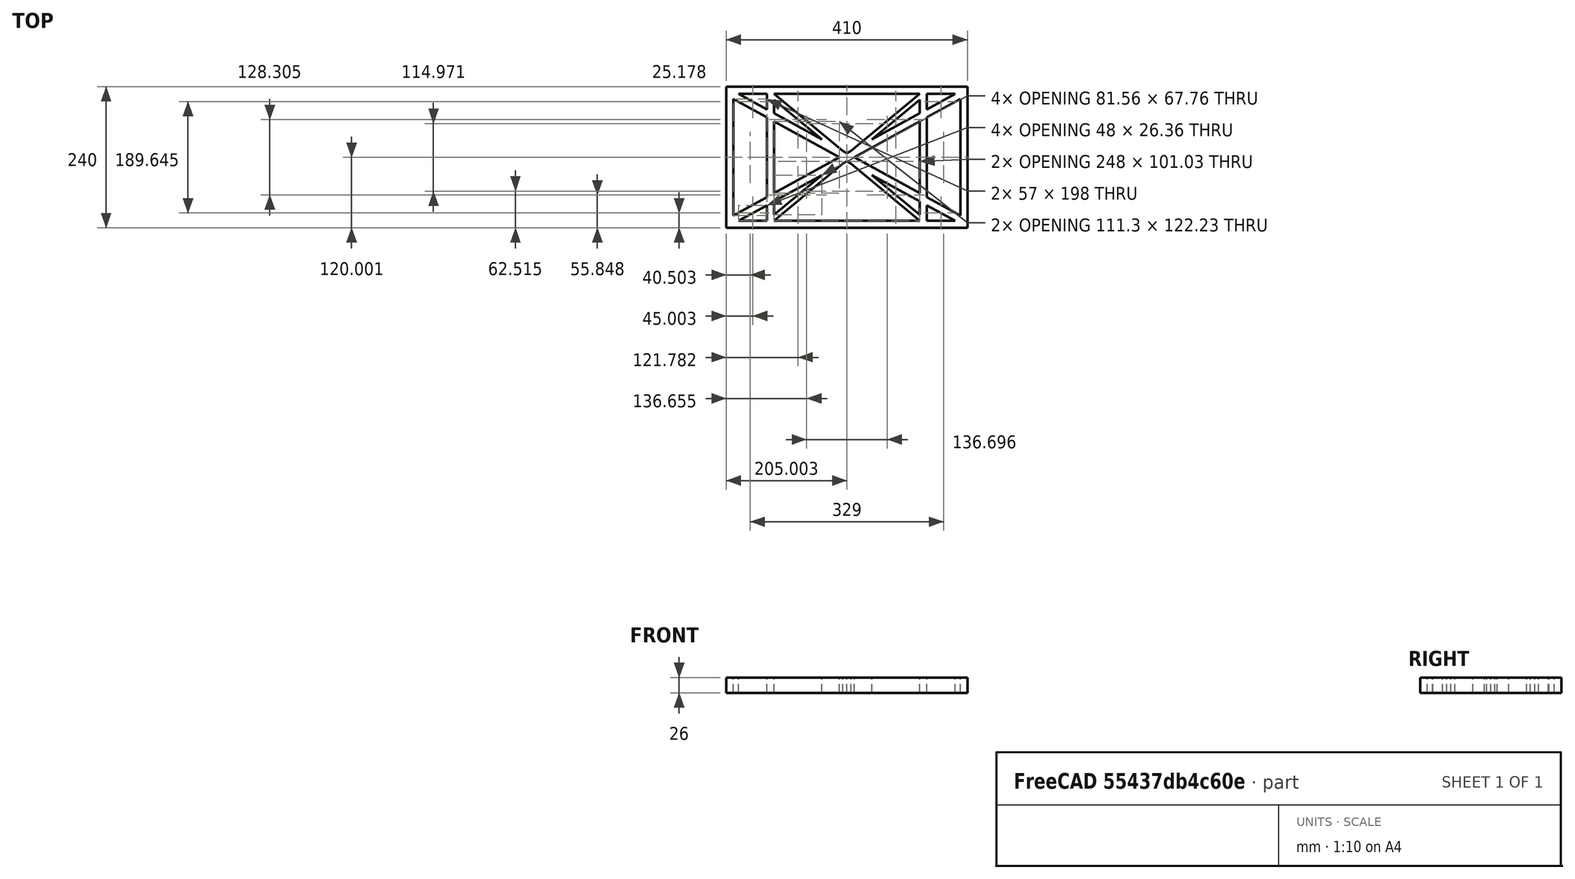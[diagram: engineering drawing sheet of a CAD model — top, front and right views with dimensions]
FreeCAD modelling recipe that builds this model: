
FCSTD DOCUMENT  (FreeCAD 0.19R0.19.2)
Label: laptopStand018
License: All rights reserved
LicenseURL: http://en.wikipedia.org/wiki/All_rights_reserved
objects: Sketcher::SketchObject×3, Part::Extrusion×1
note: 4 computed .brp shape members not serialized (recipe doc carries the construction recipe); baked Part::Feature solids carry a one-line shape summary decoded from their .brp

FEATURE [Sketcher::SketchObject] Sketch
  FullyConstrained = true
  sketch-geometry (52):
    g0: LineSegment StartX=-22.9272 StartY=136.221 StartZ=0 EndX=-22.9272 EndY=-103.779 EndZ=0
    g1: LineSegment StartX=-22.9272 StartY=136.221 StartZ=0 EndX=387.073 EndY=136.221 EndZ=0
    g2: LineSegment StartX=-22.9272 StartY=-103.779 StartZ=0 EndX=387.073 EndY=-103.779 EndZ=0
    g3: LineSegment StartX=387.073 StartY=136.221 StartZ=0 EndX=387.073 EndY=-103.779 EndZ=0
    g4: LineSegment StartX=375.073 StartY=115.221 StartZ=0 EndX=318.073 EndY=83.9235 EndZ=0
    g5: LineSegment StartX=-10.9272 StartY=-82.7794 StartZ=0 EndX=46.0728 EndY=-51.4823 EndZ=0
    g6: LineSegment StartX=-1.92719 StartY=124.221 StartZ=0 EndX=46.0728 EndY=97.8651 EndZ=0
    g7: LineSegment StartX=366.073 StartY=-91.7794 StartZ=0 EndX=318.073 EndY=-65.424 EndZ=0
    g8: LineSegment StartX=-10.9272 StartY=115.221 StartZ=0 EndX=-10.9272 EndY=-82.7794 EndZ=0
    g9: LineSegment StartX=375.073 StartY=-82.7794 StartZ=0 EndX=375.073 EndY=115.221 EndZ=0
    g10: LineSegment StartX=-1.92719 StartY=-91.7794 StartZ=0 EndX=46.0728 EndY=-91.7794 EndZ=0
    g11: LineSegment StartX=318.073 StartY=124.221 StartZ=0 EndX=366.073 EndY=124.221 EndZ=0
    g12: LineSegment StartX=306.073 StartY=-81.8102 StartZ=0 EndX=224.513 EndY=-14.0532 EndZ=0
    g13: LineSegment StartX=58.0728 StartY=114.251 StartZ=0 EndX=139.632 EndY=46.4944 EndZ=0
    g14: LineSegment StartX=306.073 StartY=124.221 StartZ=0 EndX=189.124 EndY=27.0628 EndZ=0
    g15: LineSegment StartX=58.0728 StartY=-91.7794 StartZ=0 EndX=175.022 EndY=5.37834 EndZ=0
    g16: LineSegment StartX=46.0728 StartY=124.221 StartZ=0 EndX=46.0728 EndY=97.8651 EndZ=0
    g17: LineSegment StartX=58.0728 StartY=-81.8102 StartZ=0 EndX=58.0728 EndY=-58.8351 EndZ=0
    g18: LineSegment StartX=318.073 StartY=124.221 StartZ=0 EndX=318.073 EndY=97.8651 EndZ=0
    g19: LineSegment StartX=306.073 StartY=114.251 StartZ=0 EndX=306.073 EndY=91.2763 EndZ=0
    g20: LineSegment StartX=182.073 StartY=23.1914 StartZ=0 EndX=189.124 EndY=27.0628 EndZ=0
    g21: LineSegment StartX=182.073 StartY=9.24976 StartZ=0 EndX=175.022 EndY=5.37834 EndZ=0
    g22: LineSegment StartX=224.513 StartY=46.4944 StartZ=0 EndX=306.073 EndY=114.251 EndZ=0
    g23: LineSegment StartX=175.022 StartY=27.0628 StartZ=0 EndX=58.0728 EndY=124.221 EndZ=0
    g24: LineSegment StartX=169.377 StartY=16.2206 StartZ=0 EndX=58.0728 EndY=77.3346 EndZ=0
    g25: LineSegment StartX=139.632 StartY=-14.0532 StartZ=0 EndX=58.0728 EndY=-81.8102 EndZ=0
    g26: LineSegment StartX=194.768 StartY=16.2206 StartZ=0 EndX=306.073 EndY=-44.8935 EndZ=0
    g27: LineSegment StartX=224.513 StartY=46.4944 StartZ=0 EndX=306.073 EndY=91.2763 EndZ=0
    g28: LineSegment StartX=175.022 StartY=27.0628 StartZ=0 EndX=182.073 EndY=23.1914 EndZ=0
    g29: LineSegment StartX=139.632 StartY=-14.0532 StartZ=0 EndX=58.0728 EndY=-58.8351 EndZ=0
    g30: LineSegment StartX=189.124 StartY=5.37834 StartZ=0 EndX=182.073 EndY=9.24976 EndZ=0
    g31: LineSegment StartX=189.124 StartY=5.37834 StartZ=0 EndX=306.073 EndY=-91.7794 EndZ=0
    g32: LineSegment StartX=306.073 StartY=77.3346 StartZ=0 EndX=306.073 EndY=-44.8935 EndZ=0
    g33: LineSegment StartX=318.073 StartY=83.9235 StartZ=0 EndX=318.073 EndY=-51.4823 EndZ=0
    g34: LineSegment StartX=318.073 StartY=97.8651 StartZ=0 EndX=366.073 EndY=124.221 EndZ=0
    g35: LineSegment StartX=306.073 StartY=77.3346 StartZ=0 EndX=194.768 EndY=16.2206 EndZ=0
    g36: LineSegment StartX=306.073 StartY=-58.8351 StartZ=0 EndX=224.513 EndY=-14.0532 EndZ=0
    g37: LineSegment StartX=306.073 StartY=-58.8351 StartZ=0 EndX=306.073 EndY=-81.8102 EndZ=0
    g38: LineSegment StartX=318.073 StartY=-51.4823 StartZ=0 EndX=375.073 EndY=-82.7794 EndZ=0
    g39: LineSegment StartX=318.073 StartY=-65.424 StartZ=0 EndX=318.073 EndY=-91.7794 EndZ=0
    g40: LineSegment StartX=306.073 StartY=124.221 StartZ=0 EndX=58.0728 EndY=124.221 EndZ=0
    g41: LineSegment StartX=318.073 StartY=-91.7794 StartZ=0 EndX=366.073 EndY=-91.7794 EndZ=0
    g42: LineSegment StartX=58.0728 StartY=-91.7794 StartZ=0 EndX=306.073 EndY=-91.7794 EndZ=0
    g43: LineSegment StartX=58.0728 StartY=-44.8935 StartZ=0 EndX=58.0728 EndY=77.3346 EndZ=0
    g44: LineSegment StartX=46.0728 StartY=-65.424 StartZ=0 EndX=-1.92719 EndY=-91.7794 EndZ=0
    g45: LineSegment StartX=46.0728 StartY=-65.424 StartZ=0 EndX=46.0728 EndY=-91.7794 EndZ=0
    g46: LineSegment StartX=58.0728 StartY=-44.8935 StartZ=0 EndX=169.377 EndY=16.2206 EndZ=0
    g47: LineSegment StartX=58.0728 StartY=91.2763 StartZ=0 EndX=58.0728 EndY=114.251 EndZ=0
    g48: LineSegment StartX=46.0728 StartY=83.9235 StartZ=0 EndX=46.0728 EndY=-51.4823 EndZ=0
    g49: LineSegment StartX=46.0728 StartY=124.221 StartZ=0 EndX=-1.92719 EndY=124.221 EndZ=0
    g50: LineSegment StartX=58.0728 StartY=91.2763 StartZ=0 EndX=139.632 EndY=46.4944 EndZ=0
    g51: LineSegment StartX=46.0728 StartY=83.9235 StartZ=0 EndX=-10.9272 EndY=115.221 EndZ=0
  constraints (102):
    c: Vertical(g0)
    c: Distance(g0) = 240
    c: Horizontal(g1)
    c: Distance(g1) = 410
    c: Coincident(g1,g0)
    c: Coincident(g2,g0)
    c: Horizontal(g2)
    c: Coincident(g3,g1)
    c: Vertical(g3)
    c: Coincident(g2,g3)
    c: Block(g1)
    c: Horizontal(g10)
    c: Horizontal(g11)
    c: PointOnObject(g35,g6)
    c: Coincident(g28,g20)
    c: Coincident(g30,g21)
    c: Tangent(g7,g24)
    c: PointOnObject(g24,g5)
    c: PointOnObject(g26,g4)
    c: Coincident(g20,g14)
    c: Tangent(g20,g27)
    c: Coincident(g50,g13)
    c: Coincident(g28,g23)
    c: Coincident(g22,g27)
    c: Coincident(g21,g15)
    c: Coincident(g29,g25)
    c: Tangent(g21,g29)
    c: Coincident(g36,g12)
    c: Coincident(g31,g30)
    c: Coincident(g22,g19)
    c: Tangent(g19,g32)
    c: Tangent(g18,g33)
    c: Coincident(g27,g19)
    c: Tangent(g27,g34)
    c: Coincident(g4,g33)
    c: Coincident(g35,g32)
    c: Tangent(g4,g35)
    c: Coincident(g37,g12)
    c: Tangent(g7,g36)
    c: Tangent(g32,g37)
    c: Coincident(g26,g32)
    c: Tangent(g26,g38)
    c: Coincident(g33,g38)
    c: Coincident(g39,g7)
    c: Tangent(g33,g39)
    c: Coincident(g25,g17)
    c: Tangent(g17,g43)
    c: Coincident(g29,g17)
    c: Tangent(g29,g44)
    c: Coincident(g45,g44)
    c: Tangent(g16,g45)
    c: Coincident(g5,g48)
    c: Coincident(g46,g43)
    c: Tangent(g5,g46)
    c: Tangent(g43,g47)
    c: Tangent(g16,g48)
    c: Coincident(g13,g47)
    c: PointOnObject(g40,g23)
    c: Tangent(g40,g49)
    c: Coincident(g6,g16)
    c: Coincident(g50,g47)
    c: Tangent(g6,g50)
    c: Coincident(g24,g43)
    c: Coincident(g51,g48)
    c: Tangent(g24,g51)
    c: Block(g23)
    c: Block(g14)
    c: Block(g20)
    c: Block(g40)
    c: Block(g18)
    c: Block(g34)
    c: Block(g4)
    c: Block(g38)
    c: Block(g9)
    c: Block(g36)
    c: Block(g37)
    c: Block(g7)
    c: Block(g39)
    c: Block(g22)
    c: Block(g31)
    c: Block(g42)
    c: Block(g21)
    c: Block(g15)
    c: Block(g29)
    c: Block(g25)
    c: Block(g45)
    c: Block(g44)
    c: Block(g5)
    c: Block(g8)
    c: Block(g51)
    c: Block(g6)
    c: Block(g16)
    c: Block(g13)
    c: Block(g47)
    c: Block(g35)
    c: Block(g32)
    c: Block(g24)
    c: Block(g46)
    c: Block(g49)
    c: Block(g11)
    c: Block(g41)
    c: Block(g10)
FEATURE [Part::Extrusion] Extrude
  Base = -> Sketch
  Dir = (0,0,1)
  DirMode = 2
  FaceMakerClass = Part::FaceMakerBullseye
  LengthFwd = 26
  LengthRev = 0
  Solid = true
  Symmetric = false
FEATURE [Sketcher::SketchObject] Sketch001
  FullyConstrained = false
  MapMode = 4
  Placement = pos=(0,0,0) rot=(0.57735,0.57735,0.57735;2.0944rad)
  Support = -> [Sketch]
  sketch-geometry (20):
    g0: LineSegment StartX=18.764 StartY=-18.9858 StartZ=0 EndX=18.764 EndY=-21.9858 EndZ=0
    g1: Circle CenterX=118.764 CenterY=-21.9858 CenterZ=0 NormalX=0 NormalY=0 NormalZ=1 AngleXU=0 Radius=1
    g2: Circle CenterX=98.764 CenterY=-21.9858 CenterZ=0 NormalX=0 NormalY=0 NormalZ=1 AngleXU=0 Radius=1
    g3: Circle CenterX=96.1988 CenterY=-29.0335 CenterZ=0 NormalX=0 NormalY=0 NormalZ=1 AngleXU=0 Radius=1
    g4: BSplineCurve PolesCount=3 KnotsCount=2 Degree=2 IsPeriodic=0
    g5: GeomPoint X=118.764 Y=-21.9858 Z=0
    g6: GeomPoint X=96.1988 Y=-29.0335 Z=0
    g7-g10: Circle x4 (B-spline internal-alignment scaffolding for g11; pole/knot coordinates omitted)
    g11: BSplineCurve PolesCount=4 KnotsCount=2 Degree=3 IsPeriodic=0
    g12: GeomPoint X=40.4536 Y=-21.9858 Z=0
    g13: GeomPoint X=57.8884 Y=-29.0335 Z=0
    g14: LineSegment StartX=57.8884 StartY=-29.0335 StartZ=0 EndX=-6.03412 EndY=-204.659 EndZ=0
    g15: LineSegment StartX=40.4536 StartY=-21.9858 StartZ=0 EndX=18.764 EndY=-21.9858 EndZ=0
    g16: LineSegment StartX=118.764 StartY=-18.9858 StartZ=0 EndX=118.764 EndY=-21.9858 EndZ=0
    g17: LineSegment StartX=96.1988 StartY=-29.0335 StartZ=0 EndX=27.7948 EndY=-216.972 EndZ=0
    g18: LineSegment StartX=118.764 StartY=-18.9858 StartZ=0 EndX=18.764 EndY=-18.9858 EndZ=0
    g19: LineSegment StartX=-6.03412 StartY=-204.659 StartZ=0 EndX=27.7948 EndY=-216.972 EndZ=0
  constraints (42):
    c: Vertical(g0)
    c: Distance(g0) = 3
    c: Weight(g1) = 1
    c: Equal(g1,g2)
    c: Equal(g1,g3)
    c: InternalAlignment(g1,g4)
    c: InternalAlignment(g2,g4)
    c: InternalAlignment(g3,g4)
    c: InternalAlignment(g5,g4)
    c: InternalAlignment(g6,g4)
    c: Block(g4)
    c: Weight(g7) = 1
    c: Equal(g7,g8)
    c: Equal(g7,g9)
    c: Equal(g7,g10)
    c: InternalAlignment(g7-g10 -> g11) x4
    c: InternalAlignment(g13,g11)
    c: Block(g11)
    c: Coincident(g14,g11)
    c: Coincident(g15,g11)
    c: Coincident(g15,g0)
    c: Horizontal(g15)
    c: Coincident(g16,g4)
    c: Vertical(g16)
    c: Coincident(g17,g4)
    c: Distance(g17) = 200
    c: Block(g17)
    c: Coincident(g18,g16)
    c: Coincident(g18,g0)
    c: Horizontal(g18)
    c: Distance(g18) = 100
    c: Block(g18)
    c: Block(g15)
    c: Block(g0)
    c: Block(g16)
    c: Block(g14)
    c: Coincident(g19,g14)
    c: Coincident(g19,g17)
    c: Block(g19)
    c: Angle(g17) = -1.91986
    c: Angle(g14) = -1.91986
    c: Angle(g19) = -0.349066
FEATURE [Sketcher::SketchObject] Sketch002
  FullyConstrained = true
  Placement = pos=(0,0,0) rot=(-1,0,0;4.71239rad)
